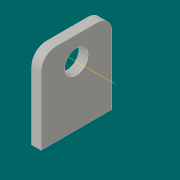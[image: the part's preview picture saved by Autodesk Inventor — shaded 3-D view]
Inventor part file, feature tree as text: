
AUTODESK INVENTOR PART (.ipt)
format: ipt  version: 2016 (Build 200138000, 138)  size: 89,088 bytes
history: native  units: in
note: dims shown in document units (in); Inventor stores cm internally (conversion verified against a paired STEP export)
features: extrude x1, fillet x1, other x1, sketch x1
ambient origin geometry x8: Origin, YZ Plane, XZ Plane, XY Plane, X Axis, Y Axis, Z Axis, Center Point
bodies: Solid1 (feature_tree)
feature tree (4):
  extrude  "Extrusion1"  Depth=0.6in
  fillet  "Fillet1"  Radius=0.7in
  other  "Work Axis1"
  sketch  "Sketch1"  dims[d0=0.2in d1=0.6in d2=0.7in d3=0.08in d4=0.0in d5=0.2in d6=0.125in]
